# Revit family: FR_PG-EVO_Fondation_V3_6
name_source: partatom
category: Allgemeines Modell
revit_build: Autodesk Revit 2018 (Build: 20181015_0930(x64)
units: mm (PartAtom-declared; Revit-internal decimal feet)

## family parameters
Beim Laden mit Abzugskörper schneiden = Ja
Bemaßung runder Anschluss = Durchmesser verwenden
Gemeinsam genutzt = Ja
Kann Basisbauteil für Bewehrung sein = Nein
Raumberechnungspunkt = Nein
Teiletyp = Normal

## types (1)
- MEARIN PG-EVO-V3_6 Mörtelbett
    Angle des côtés de l'approfondissement = 60.00°
    Bauelement = Caniveau de drainage surface de l'eau
    Construction Élément de drainage = Lit de mortier Caniveau en profile de peigne
    Documents de mise en œuvre = conformément aux dessins et à la description du produits
    Fiche technique produits = https://www.mea-group.com
    Hersteller = MEA Bautechnik GmbH business unite MEA Water Management
    IfcExportAs = IfcWasteTerminalType
    IfcExportType = USERDEFINED
    Largeur = 180 mm  [stored 0.590551 ft]
    Largeur d'élément de drainage = 150
    Largeur utile = 150 mm  [stored 0.492126 ft]
    MEA aide montage = https://www.mea-group.com
    Materiaux, enrobage / Fondation = PCC-Mörtel/Epoxy-Mörtel
    Poids = voir la densité de mortier
    STLB-Bau exemplaire = https://www.stlb-bau-online.de
    Technique de montage = Caniveau seul
    Type élément de drainage = Typ M
    URL = https://www.mea-group.com
    guid = cf6c1bd8-9bf4-4563-8c57-07955e2378ac
    max. Hauteur de sol = 40mm
    min. Hauteur de sol = 60mm
    élement de contruction, de drainage = Caniveau de drainage

note: [stored X ft] marks values corroborated as IEEE doubles in the binary element streams (Revit-internal decimal feet)
